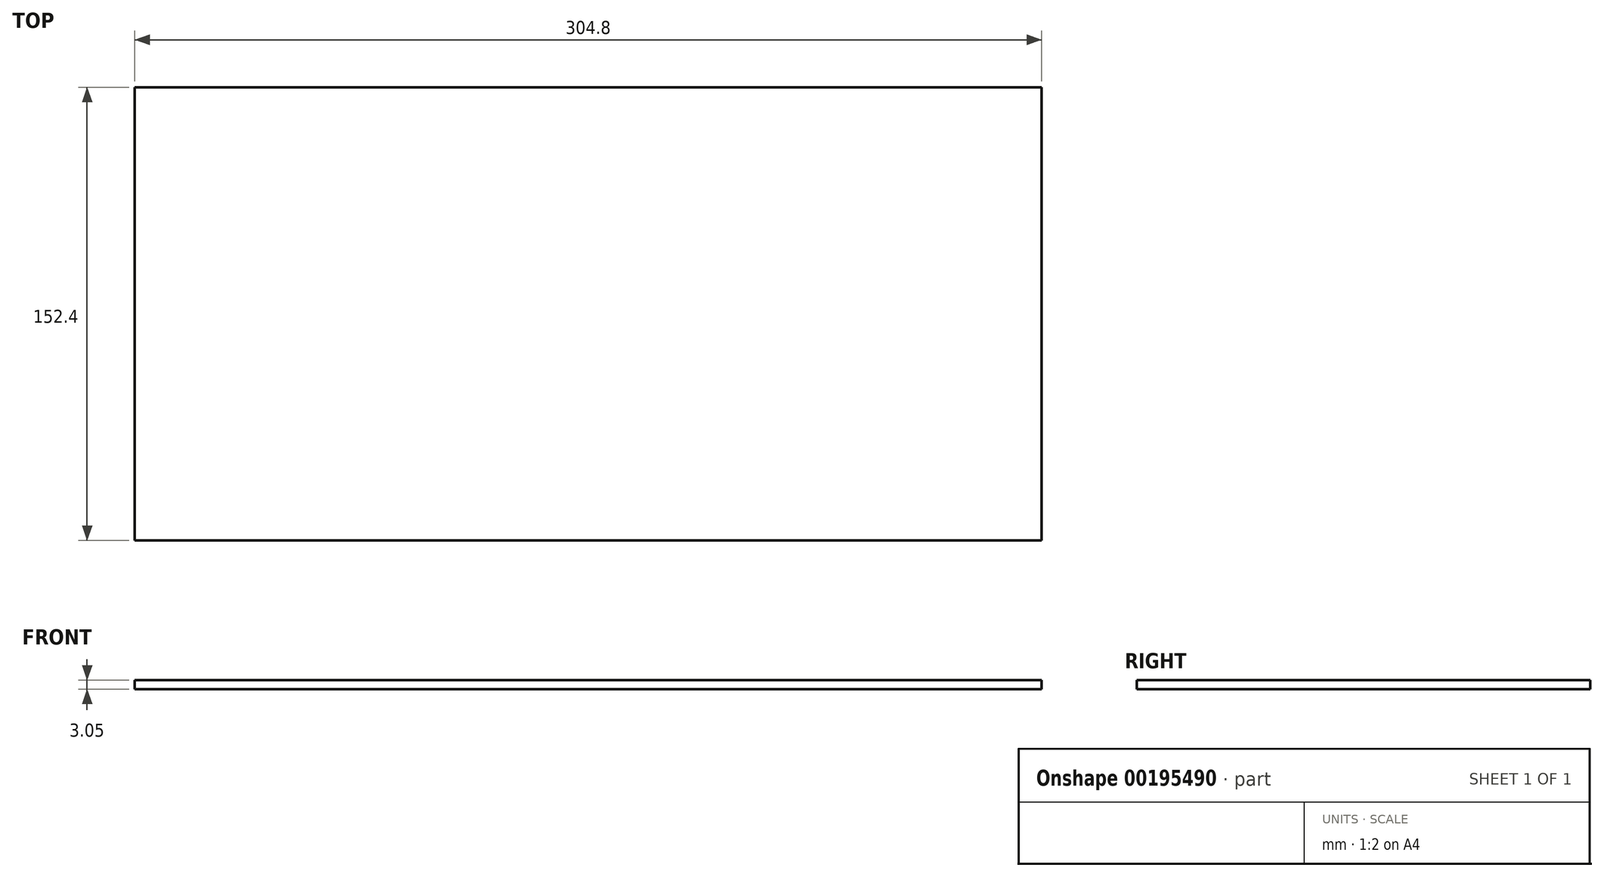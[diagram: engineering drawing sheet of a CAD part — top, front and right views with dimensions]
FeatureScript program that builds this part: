
annotation { "Feature Type Name" : "Feature", "Feature Type Description" : "" }
export const myFeature = defineFeature(function(context is Context, id is Id, definition is map)
    precondition{}
    {
        {
            var Q0;
            Q0=qCreatedBy(makeId("Top.planeOp"),FACE);
            var sketch = newSketch(context, id + "F0", { "sketchPlane" : qUnion([Q0])});
            skLineSegment(sketch, "E0.bottom", {"start": v(152.4, 76.2) * mm, "end": v(-152.4, 76.2) * mm});
            skLineSegment(sketch, "E0.top", {"start": v(152.4, -76.2) * mm, "end": v(-152.4, -76.2) * mm});
            skLineSegment(sketch, "E0.left", {"start": v(152.4, 76.2) * mm, "end": v(152.4, -76.2) * mm});
            skLineSegment(sketch, "E0.right", {"start": v(-152.4, 76.2) * mm, "end": v(-152.4, -76.2) * mm});
            skPoint(sketch, "E0.middle", {"position": v(0, 0) * mm});
            skSolve(sketch);
        }
        {
            var Q0;
            Q0 = qSketchRegion(id + "F0", true);
            extrude(context, id + "F1", {"entities" : qUnion([Q0]), "depth" : 3.05 * mm});
        }
    });
